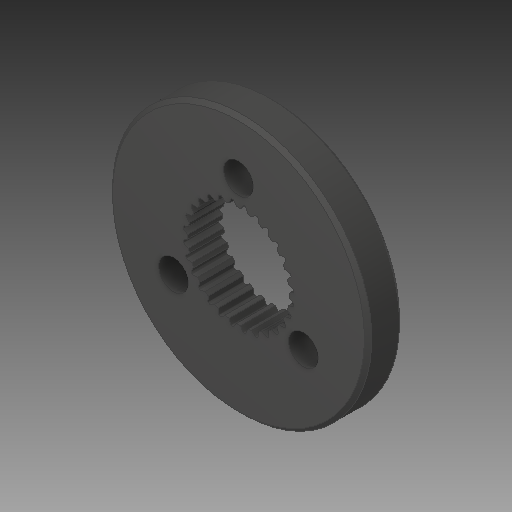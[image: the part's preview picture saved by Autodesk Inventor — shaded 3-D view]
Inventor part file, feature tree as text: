
AUTODESK INVENTOR PART (.ipt)
format: ipt  version: 2018 (Build 220112000, 112)  size: 273,920 bytes
history: native  units: in
note: dims shown in document units (in); Inventor stores cm internally (conversion verified against a paired STEP export)
features: chamfer x1
ambient origin geometry x8: Origin, YZ Plane, XZ Plane, XY Plane, X Axis, Y Axis, Z Axis, Center Point
bodies: Solid1 (feature_tree)
feature tree (1):
  chamfer  "Chamfer1"  [1 undecoded]
note: 1 required parameter value undecoded (feature->parameter linkage not recoverable at this tier; creation-order binding heuristic only, values carry confidence <= 0.55)
